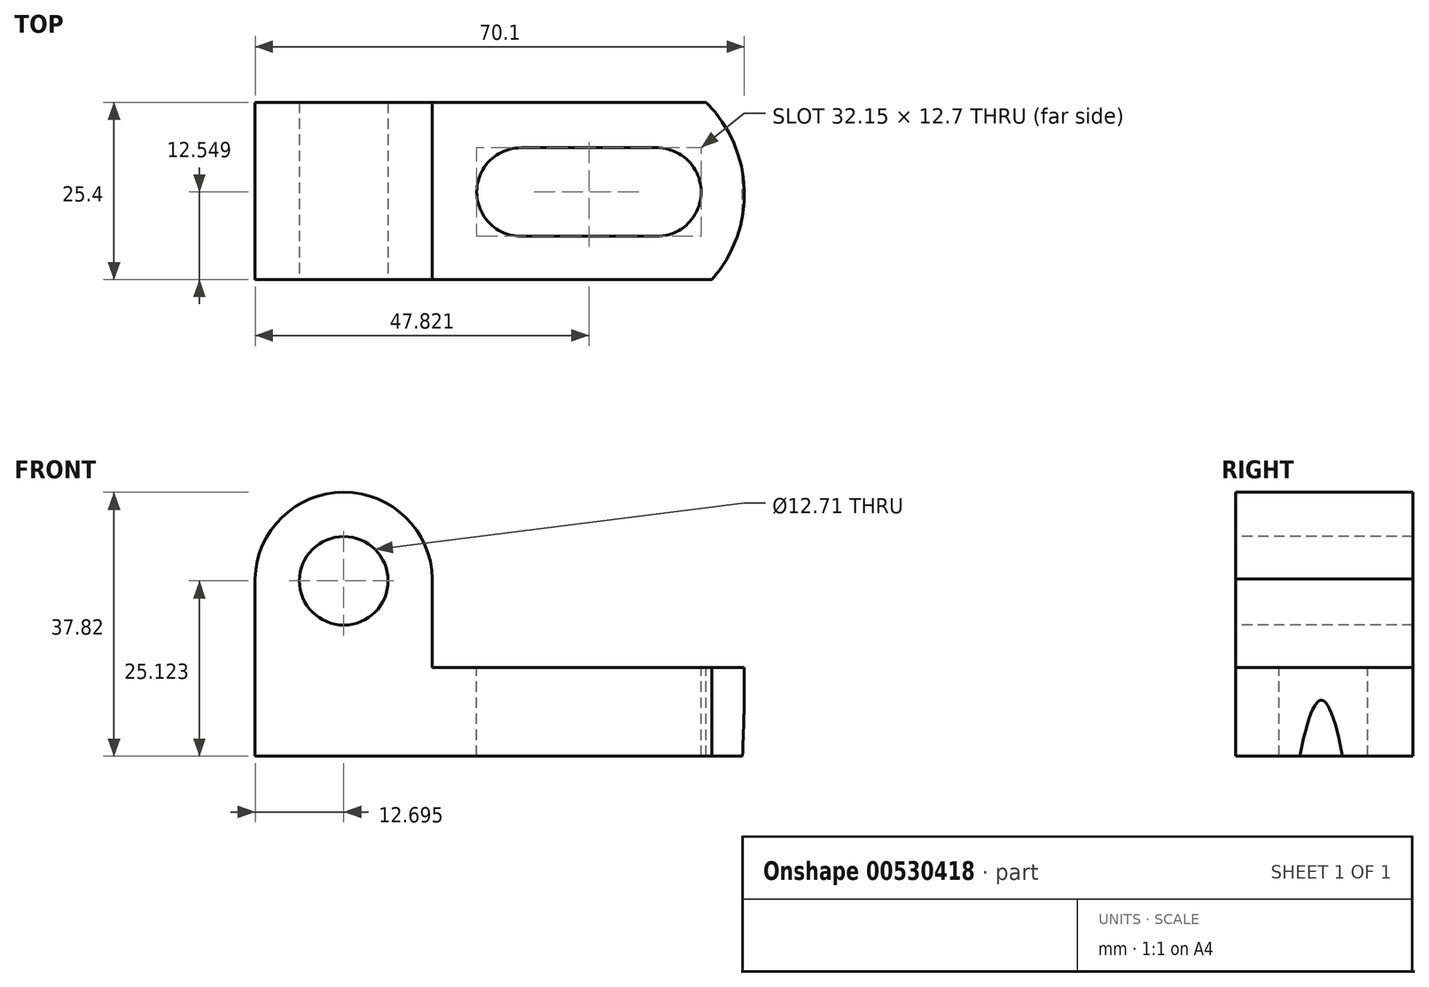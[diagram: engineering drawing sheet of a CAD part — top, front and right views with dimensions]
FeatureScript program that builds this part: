
annotation { "Feature Type Name" : "Feature", "Feature Type Description" : "" }
export const myFeature = defineFeature(function(context is Context, id is Id, definition is map)
    precondition{}
    {
        {
            var Q0;
            Q0=qCreatedBy(makeId("Front.planeOp"),FACE);
            var sketch = newSketch(context, id + "F0", { "sketchPlane" : qUnion([Q0])});
            skLineSegment(sketch, "E0", {"start": v(-45.42, 38.1) * mm, "end": v(-45.42, 0) * mm});
            skLineSegment(sketch, "E1", {"start": v(-45.42, 0) * mm, "end": v(24.43, 0) * mm});
            skLineSegment(sketch, "E2", {"start": v(-45.42, 38.1) * mm, "end": v(-20.02, 38.1) * mm});
            skLineSegment(sketch, "E3", {"start": v(-20.02, 38.1) * mm, "end": v(-20.02, 12.7) * mm});
            skLineSegment(sketch, "E4", {"start": v(-20.02, 12.7) * mm, "end": v(24.83, 12.7) * mm});
            skLineSegment(sketch, "E5", {"start": v(24.83, 12.7) * mm, "end": v(24.43, 0) * mm});
            skSolve(sketch);
        }
        {
            var Q0;
            Q0=makeQuery(id+"F0.imprint","IMPRINT",FACE,{"disambiguationData":[TD([[makeQuery(id+"F0.imprint","IMPRINT",EDGE,{"derivedFrom":sQuery(id+"F0.wireOp",EDGE,"E0")}),1.0]])]});
            extrude(context, id + "F1", {"entities" : qUnion([Q0]), "depth" : 25.4 * mm, "offsetDistance" : 25.4 * mm});
        }
        {
            var Q0;
            Q0=makeQuery(id+"F1.opExtrude","CAP_FACE",FACE,{"disambiguationData":[OSD([sQuery(id+"F0.wireOp",EDGE,"E0"),sQuery(id+"F0.wireOp",EDGE,"E1"),sQuery(id+"F0.wireOp",EDGE,"E2"),sQuery(id+"F0.wireOp",EDGE,"E3"),sQuery(id+"F0.wireOp",EDGE,"E4"),sQuery(id+"F0.wireOp",EDGE,"E5")])],"isStart":false});
            var sketch = newSketch(context, id + "F2", { "sketchPlane" : qUnion([Q0])});
            skArc(sketch, "E6", {"start": v(-20.02, 25.4) * mm, "mid": v(-32.72, 37.82) * mm, "end": v(-45.42, 25.4) * mm});
            skSolve(sketch);
        }
        {
            var Q0;
            {var subQ0=sQuery(id+"F2.wireOp",EDGE,"E6");Q0=makeQuery(id+"F2.imprint","IMPRINT",FACE,{"disambiguationData":[TD([[makeQuery(id+"F2.imprint","IMPRINT",EDGE,{"derivedFrom":subQ0}),-1.0]])]});}
            extrude(context, id + "F3", {"entities" : qUnion([Q0]), "operationType" : NewBodyOperationType.REMOVE, "endBound" : BoundingType.THROUGH_ALL, "oppositeDirection" : true, "depth" : 25.4 * mm, "offsetDistance" : 25.4 * mm});
        }
        {
            var Q0;
            Q0=makeQuery(id+"F1.opExtrude","CAP_FACE",FACE,{"disambiguationData":[OSD([sQuery(id+"F0.wireOp",EDGE,"E0"),sQuery(id+"F0.wireOp",EDGE,"E1"),sQuery(id+"F0.wireOp",EDGE,"E2"),sQuery(id+"F0.wireOp",EDGE,"E3"),sQuery(id+"F0.wireOp",EDGE,"E4"),sQuery(id+"F0.wireOp",EDGE,"E5")])],"isStart":false});
            var sketch = newSketch(context, id + "F4", { "sketchPlane" : qUnion([Q0])});
            skCircle(sketch, "E7", {"center": v(-32.72, 25.12) * mm, "radius": 6.35 * mm});
            skSolve(sketch);
        }
        {
            var Q0;
            Q0=makeQuery(id+"F4.imprint","IMPRINT",FACE,{"disambiguationData":[TD([[makeQuery(id+"F4.imprint","IMPRINT",EDGE,{"derivedFrom":sQuery(id+"F4.wireOp",EDGE,"E7")}),1.0]])]});
            extrude(context, id + "F5", {"entities" : qUnion([Q0]), "operationType" : NewBodyOperationType.REMOVE, "endBound" : BoundingType.THROUGH_ALL, "oppositeDirection" : true, "depth" : 25.4 * mm, "offsetDistance" : 25.4 * mm});
        }
        {
            var Q0;
            Q0=makeQuery(id+"F1.opExtrude","SWEPT_FACE",FACE,{"disambiguationData":[OSD([sQuery(id+"F0.wireOp",EDGE,"E4")])]});
            var sketch = newSketch(context, id + "F6", { "sketchPlane" : qUnion([Q0])});
            skSolve(sketch);
        }
        {
            var Q0;
            {var subQ0=sQuery(id+"F0.wireOp",EDGE,"E4");Q0=makeQuery(id+"F6.imprint","IMPRINT",FACE,{"disambiguationData":[TD([[makeQuery(id+"F6.imprint","IMPRINT",EDGE,{"derivedFrom":makeQuery(id+"F1.opExtrude","CAP_EDGE",EDGE,{"disambiguationData":[OSD([subQ0])],"isStart":true})}),-1.0]])]});}
            var sketch = newSketch(context, id + "F7", { "sketchPlane" : qUnion([Q0])});
            skCircle(sketch, "E8", {"center": v(-7.32, -12.85) * mm, "radius": 6.35 * mm});
            skCircle(sketch, "E9", {"center": v(12.13, -12.85) * mm, "radius": 6.35 * mm});
            skLineSegment(sketch, "E10", {"start": v(-7.32, -6.5) * mm, "end": v(12.13, -6.5) * mm});
            skLineSegment(sketch, "E11", {"start": v(-7.32, -19.2) * mm, "end": v(12.13, -19.2) * mm});
            skArc(sketch, "E12", {"start": v(20, -25.43) * mm, "mid": v(24.67, -12.55) * mm, "end": v(19.2, 0) * mm});
            skSolve(sketch);
        }
        {
            var Q0;
            Q0 = qSketchRegion(id + "F7", true);
            extrude(context, id + "F8", {"entities" : qUnion([Q0]), "operationType" : NewBodyOperationType.REMOVE, "oppositeDirection" : true, "depth" : 25.4 * mm, "offsetDistance" : 25.4 * mm});
        }
        {
            var Q0;
            {var subQ1=sQuery(id+"F0.wireOp",EDGE,"E4");var subQ6=makeQuery(id+"F6.imprint","IMPRINT",EDGE,{"derivedFrom":makeQuery(id+"F1.opExtrude","SWEPT_EDGE",EDGE,{"disambiguationData":[OSD([subQ1,sQuery(id+"F0.wireOp",EDGE,"E5")])]})});Q0=makeQuery(id+"F7.imprint","IMPRINT",FACE,{"disambiguationData":[TD([[makeQuery(id+"F7.imprint","IMPRINT",EDGE,{"derivedFrom":subQ6}),1.0]])]});}
            extrude(context, id + "F9", {"entities" : qUnion([Q0]), "operationType" : NewBodyOperationType.REMOVE, "oppositeDirection" : true, "depth" : 25.4 * mm, "offsetDistance" : 25.4 * mm});
        }
    });
